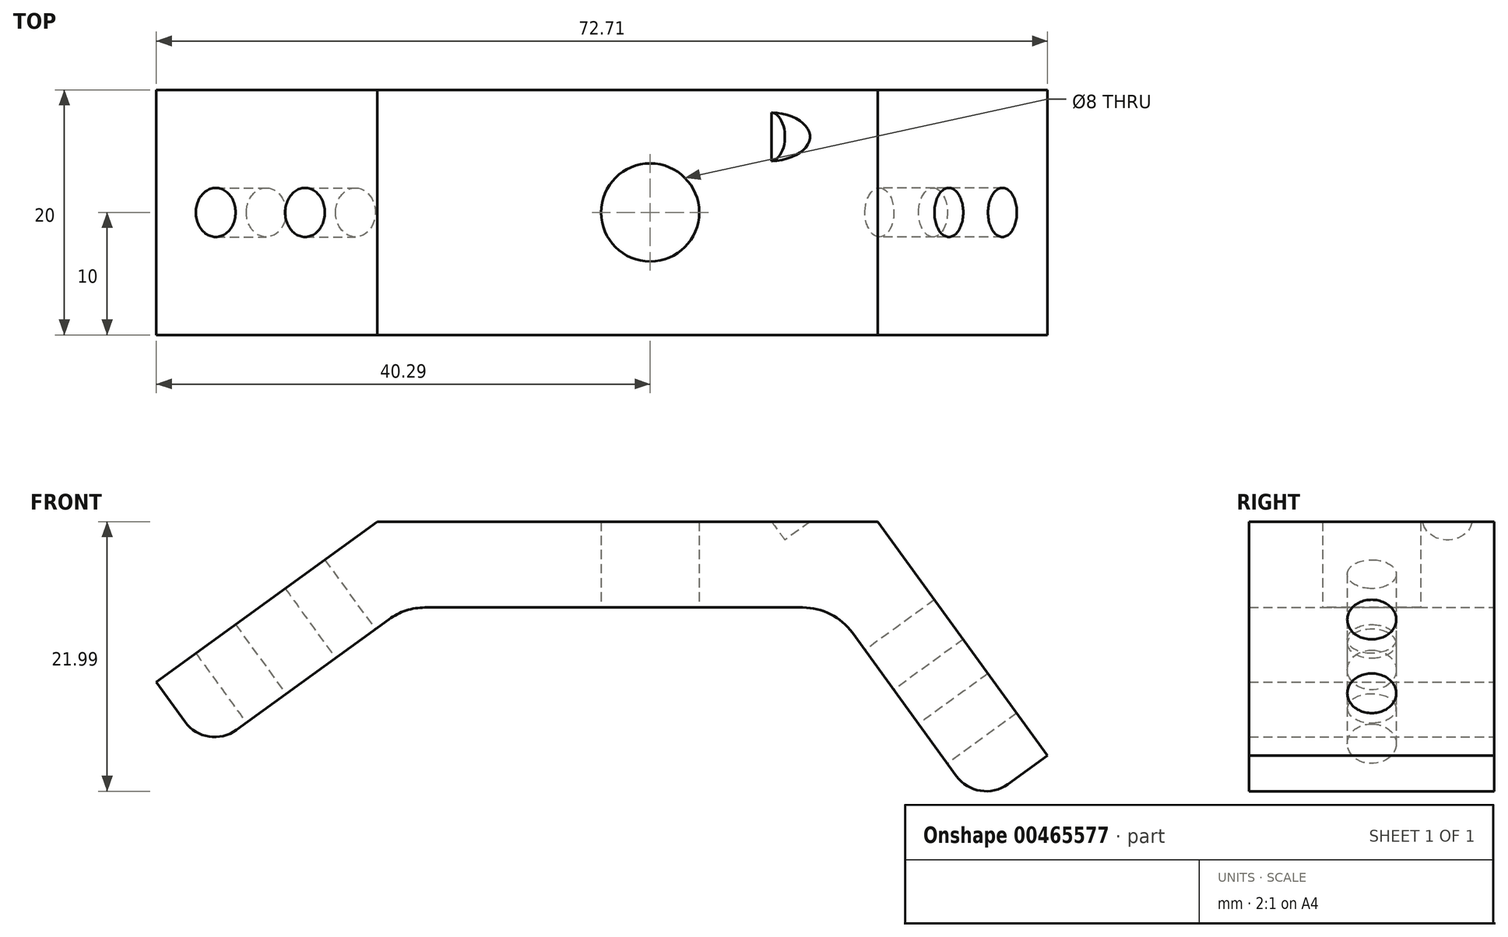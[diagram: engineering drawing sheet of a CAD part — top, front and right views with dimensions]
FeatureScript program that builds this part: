
annotation { "Feature Type Name" : "Feature", "Feature Type Description" : "" }
export const myFeature = defineFeature(function(context is Context, id is Id, definition is map)
    precondition{}
    {
        {
            var Q0;
            Q0=qCreatedBy(makeId("Front.planeOp"),FACE);
            var sketch = newSketch(context, id + "F0", { "sketchPlane" : qUnion([Q0])});
            skLineSegment(sketch, "E0", {"start": v(-36.18, -11.76) * mm, "end": v(-20, 0) * mm});
            skLineSegment(sketch, "E1", {"start": v(-20, 0) * mm, "end": v(15, 0) * mm});
            skLineSegment(sketch, "E2", {"start": v(15, 0) * mm, "end": v(26.76, -16.18) * mm});
            skLineSegment(sketch, "E3.0", {"start": v(18.57, 7) * mm, "end": v(32.42, -12.07) * mm});
            skLineSegment(sketch, "E3.1", {"start": v(-22.27, 7) * mm, "end": v(18.57, 7) * mm});
            skLineSegment(sketch, "E3.2", {"start": v(-40.3, -6.1) * mm, "end": v(-22.27, 7) * mm});
            skLineSegment(sketch, "E4", {"start": v(-40.3, -6.1) * mm, "end": v(-36.18, -11.76) * mm});
            skLineSegment(sketch, "E5", {"start": v(26.76, -16.18) * mm, "end": v(32.42, -12.07) * mm});
            skSolve(sketch);
        }
        {
            var Q0;
            Q0=qSketchRegion(id+"F0",true);
            extrude(context, id + "F1", {"entities" : qUnion([Q0]), "depth" : 10 * mm, "hasSecondDirection" : true, "secondDirectionOppositeDirection" : true, "secondDirectionDepth" : 10 * mm});
        }
        {
            var Q0;
            Q0=makeQuery(id+"F1.opExtrude","SWEPT_FACE",FACE,{"disambiguationData":[OSD([sQuery(id+"F0.wireOp",EDGE,"E0")])]});
            var sketch = newSketch(context, id + "F2", { "sketchPlane" : qUnion([Q0])});
            skPoint(sketch, "E6", {"position": v(0, -37.85) * mm});
            skPoint(sketch, "E7", {"position": v(0, -24) * mm});
            skPoint(sketch, "E8", {"position": v(-30.18, 0) * mm});
            skPoint(sketch, "E9", {"position": v(-21.18, 0) * mm});
            skSolve(sketch);
        }
        {
            var Q0;
            Q0=sQuery(id+"F2.wireOp",VERTEX,"E6");
            var Q1;
            Q1=sQuery(id+"F2.wireOp",VERTEX,"E7");
            var Q2;
            Q2=sQuery(id+"F2.wireOp",VERTEX,"E8");
            var Q3;
            Q3=sQuery(id+"F2.wireOp",VERTEX,"E9");
            var Q4;
            Q4=makeQuery(id+"F1.opExtrude","SWEPT_BODY",BODY,{"disambiguationData":[OSD([sQuery(id+"F0.wireOp",EDGE,"E0"),sQuery(id+"F0.wireOp",EDGE,"E1"),sQuery(id+"F0.wireOp",EDGE,"E2"),sQuery(id+"F0.wireOp",EDGE,"E3.0"),sQuery(id+"F0.wireOp",EDGE,"E3.1"),sQuery(id+"F0.wireOp",EDGE,"E3.2"),sQuery(id+"F0.wireOp",EDGE,"E4"),sQuery(id+"F0.wireOp",EDGE,"E5")])]});
            hole(context, id + "F3", {"style" : HoleStyle.SIMPLE, "endStyle" : HoleEndStyle.THROUGH, "holeDiameter" : 4 * mm, "isTappedThrough" : true, "tappedDepth" : 12 * mm, "tapClearance" : 3, "locations" : qUnion([Q0, Q1, Q2, Q3]), "scope" : qUnion([Q4])});
        }
        {
            var Q0;
            Q0=makeQuery(id+"F1.opExtrude","SWEPT_FACE",FACE,{"disambiguationData":[OSD([sQuery(id+"F0.wireOp",EDGE,"E2")])]});
            var sketch = newSketch(context, id + "F4", { "sketchPlane" : qUnion([Q0])});
            skPoint(sketch, "E10", {"position": v(16.06, 0) * mm});
            skPoint(sketch, "E11", {"position": v(-6.17, 0) * mm});
            skPoint(sketch, "E12", {"position": v(0, -13.82) * mm});
            skPoint(sketch, "E13", {"position": v(0, -22.82) * mm});
            skSolve(sketch);
        }
        {
            var Q0;
            Q0=sQuery(id+"F4.wireOp",VERTEX,"E10");
            var Q1;
            Q1=sQuery(id+"F4.wireOp",VERTEX,"E11");
            var Q2;
            Q2=makeQuery(id+"F1.opExtrude","SWEPT_BODY",BODY,{"disambiguationData":[OSD([sQuery(id+"F0.wireOp",EDGE,"E0"),sQuery(id+"F0.wireOp",EDGE,"E1"),sQuery(id+"F0.wireOp",EDGE,"E2"),sQuery(id+"F0.wireOp",EDGE,"E3.0"),sQuery(id+"F0.wireOp",EDGE,"E3.1"),sQuery(id+"F0.wireOp",EDGE,"E3.2"),sQuery(id+"F0.wireOp",EDGE,"E4"),sQuery(id+"F0.wireOp",EDGE,"E5")])]});
            hole(context, id + "F5", {"style" : HoleStyle.SIMPLE, "endStyle" : HoleEndStyle.THROUGH, "holeDiameter" : 4 * mm, "isTappedThrough" : true, "tappedDepth" : 12 * mm, "tapClearance" : 3, "locations" : qUnion([Q0, Q1]), "scope" : qUnion([Q2])});
        }
        {
            var Q0;
            Q0=makeQuery(id+"F1.opExtrude","SWEPT_FACE",FACE,{"disambiguationData":[OSD([sQuery(id+"F0.wireOp",EDGE,"E1")])]});
            var sketch = newSketch(context, id + "F6", { "sketchPlane" : qUnion([Q0])});
            skPoint(sketch, "E14", {"position": v(0, 0) * mm});
            skSolve(sketch);
        }
        {
            var Q0;
            Q0=sQuery(id+"F6.wireOp",VERTEX,"E14");
            var Q1;
            Q1=makeQuery(id+"F1.opExtrude","SWEPT_BODY",BODY,{"disambiguationData":[OSD([sQuery(id+"F0.wireOp",EDGE,"E0"),sQuery(id+"F0.wireOp",EDGE,"E1"),sQuery(id+"F0.wireOp",EDGE,"E2"),sQuery(id+"F0.wireOp",EDGE,"E3.0"),sQuery(id+"F0.wireOp",EDGE,"E3.1"),sQuery(id+"F0.wireOp",EDGE,"E3.2"),sQuery(id+"F0.wireOp",EDGE,"E4"),sQuery(id+"F0.wireOp",EDGE,"E5")])]});
            hole(context, id + "F7", {"style" : HoleStyle.SIMPLE, "endStyle" : HoleEndStyle.THROUGH, "holeDiameter" : 8 * mm, "isTappedThrough" : true, "tappedDepth" : 12 * mm, "tapClearance" : 3, "locations" : qUnion([Q0]), "scope" : qUnion([Q1])});
        }
        {
            var Q0;
            Q0=makeQuery(id+"F1.opExtrude","SWEPT_EDGE",EDGE,{"disambiguationData":[OSD([sQuery(id+"F0.wireOp",EDGE,"E0"),sQuery(id+"F0.wireOp",EDGE,"E4")])]});
            var Q1;
            Q1=makeQuery(id+"F1.opExtrude","SWEPT_EDGE",EDGE,{"disambiguationData":[OSD([sQuery(id+"F0.wireOp",EDGE,"E2"),sQuery(id+"F0.wireOp",EDGE,"E5")])]});
            fillet(context, id + "F8", {"entities" : qUnion([Q0, Q1]), "radius" : 3 * mm, "tangentPropagation" : true, "allowEdgeOverflow" : false});
        }
        {
            var Q0;
            Q0=makeQuery(id+"F1.opExtrude","SWEPT_EDGE",EDGE,{"disambiguationData":[OSD([sQuery(id+"F0.wireOp",EDGE,"E0"),sQuery(id+"F0.wireOp",EDGE,"E1")])]});
            var Q1;
            Q1=makeQuery(id+"F1.opExtrude","SWEPT_EDGE",EDGE,{"disambiguationData":[OSD([sQuery(id+"F0.wireOp",EDGE,"E1"),sQuery(id+"F0.wireOp",EDGE,"E2")])]});
            fillet(context, id + "F9", {"entities" : qUnion([Q0, Q1]), "radius" : 5 * mm, "tangentPropagation" : true, "allowEdgeOverflow" : false});
        }
        {
            var Q0;
            Q0=makeQuery(id+"F1.opExtrude","SWEPT_FACE",FACE,{"disambiguationData":[OSD([sQuery(id+"F0.wireOp",EDGE,"E2")])]});
            var sketch = newSketch(context, id + "F10", { "sketchPlane" : qUnion([Q0])});
            skPoint(sketch, "E15", {"position": v(0, -15.11) * mm});
            skPoint(sketch, "E16", {"position": v(0, -22.55) * mm});
            skSolve(sketch);
        }
        {
            var Q0;
            Q0=sQuery(id+"F10.wireOp",VERTEX,"E15");
            var Q1;
            Q1=sQuery(id+"F10.wireOp",VERTEX,"E16");
            var Q2;
            Q2=makeQuery(id+"F1.opExtrude","SWEPT_BODY",BODY,{"disambiguationData":[OSD([sQuery(id+"F0.wireOp",EDGE,"E0"),sQuery(id+"F0.wireOp",EDGE,"E1"),sQuery(id+"F0.wireOp",EDGE,"E2"),sQuery(id+"F0.wireOp",EDGE,"E3.0"),sQuery(id+"F0.wireOp",EDGE,"E3.1"),sQuery(id+"F0.wireOp",EDGE,"E3.2"),sQuery(id+"F0.wireOp",EDGE,"E4"),sQuery(id+"F0.wireOp",EDGE,"E5")])]});
            hole(context, id + "F11", {"style" : HoleStyle.SIMPLE, "endStyle" : HoleEndStyle.THROUGH, "holeDiameter" : 4 * mm, "isTappedThrough" : true, "tappedDepth" : 12 * mm, "tapClearance" : 3, "locations" : qUnion([Q0, Q1]), "scope" : qUnion([Q2])});
        }
    });
